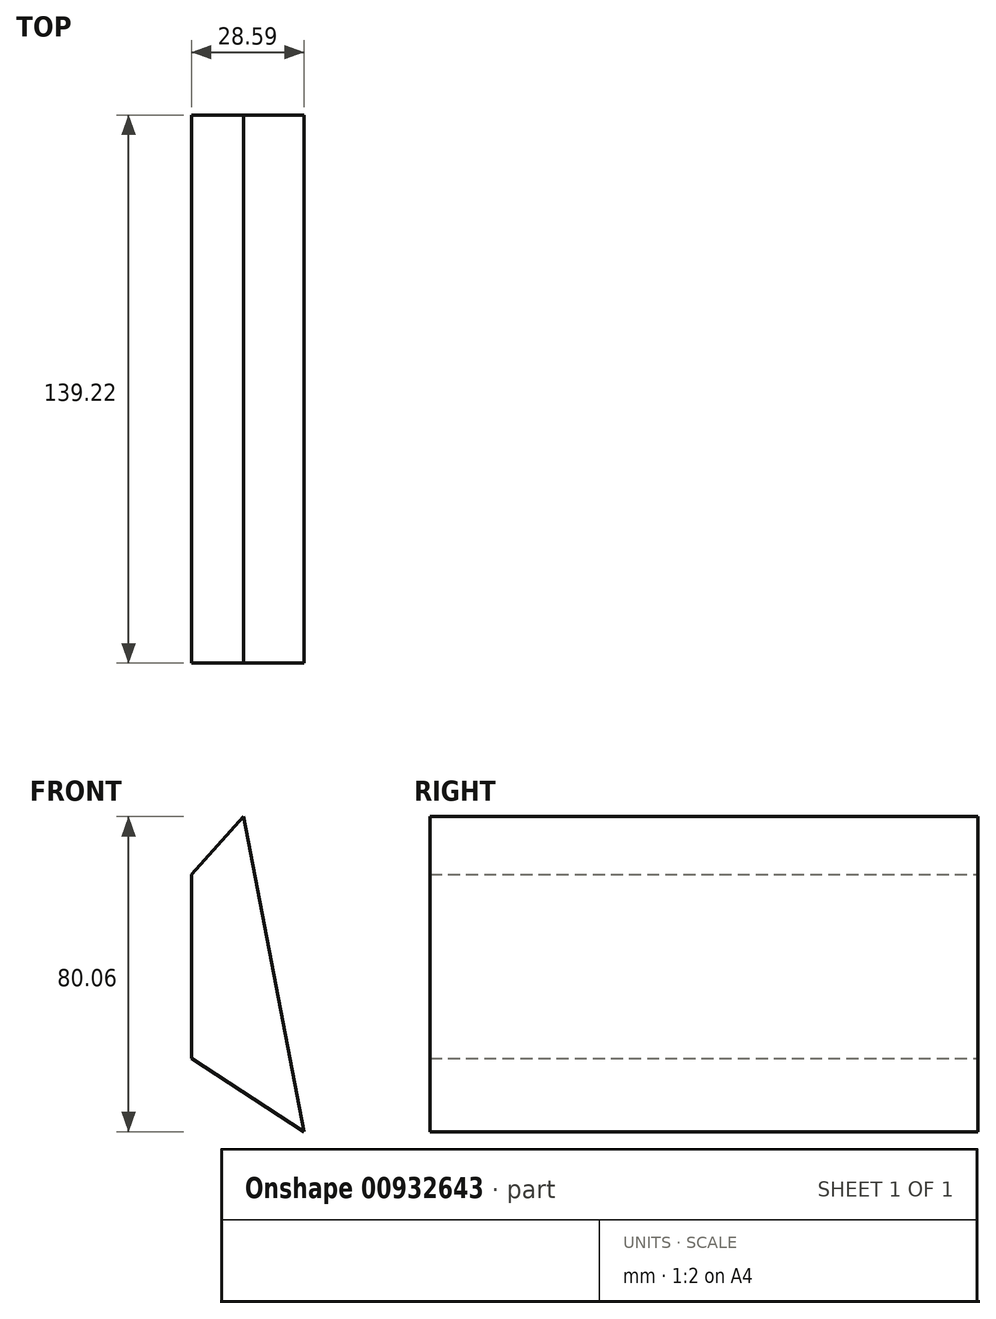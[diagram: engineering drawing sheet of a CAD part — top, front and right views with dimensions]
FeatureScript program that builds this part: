
annotation { "Feature Type Name" : "Feature", "Feature Type Description" : "" }
export const myFeature = defineFeature(function(context is Context, id is Id, definition is map)
    precondition{}
    {
        {
            var Q0;
            Q0=qCreatedBy(makeId("Front.planeOp"),FACE);
            var sketch = newSketch(context, id + "F0", { "sketchPlane" : qUnion([Q0])});
            skLineSegment(sketch, "E0", {"start": v(-52.49, 14.72) * mm, "end": v(49.07, 58.97) * mm});
            skLineSegment(sketch, "E1", {"start": v(49.07, 58.97) * mm, "end": v(49.07, -34.82) * mm});
            skLineSegment(sketch, "E2", {"start": v(49.07, -34.82) * mm, "end": v(-37.12, -65.34) * mm});
            skLineSegment(sketch, "E3", {"start": v(-37.12, -65.34) * mm, "end": v(-52.49, 14.72) * mm});
            skLineSegment(sketch, "E4", {"start": v(-65.71, -46.7) * mm, "end": v(-37.12, -65.34) * mm});
            skLineSegment(sketch, "E5", {"start": v(-52.49, 14.72) * mm, "end": v(-65.71, 0) * mm});
            skLineSegment(sketch, "E6", {"start": v(-65.71, 0) * mm, "end": v(-65.71, -46.7) * mm});
            skSolve(sketch);
        }
        {
            var Q0;
            Q0=makeQuery(id+"F0.imprint","IMPRINT",FACE,{"disambiguationData":[TD([[makeQuery(id+"F0.imprint","IMPRINT",EDGE,{"derivedFrom":sQuery(id+"F0.wireOp",EDGE,"E3")}),1.0]])]});
            extrude(context, id + "F1", {"entities" : qUnion([Q0]), "depth" : 139.22 * mm, "offsetDistance" : 25.4 * mm});
        }
    });
